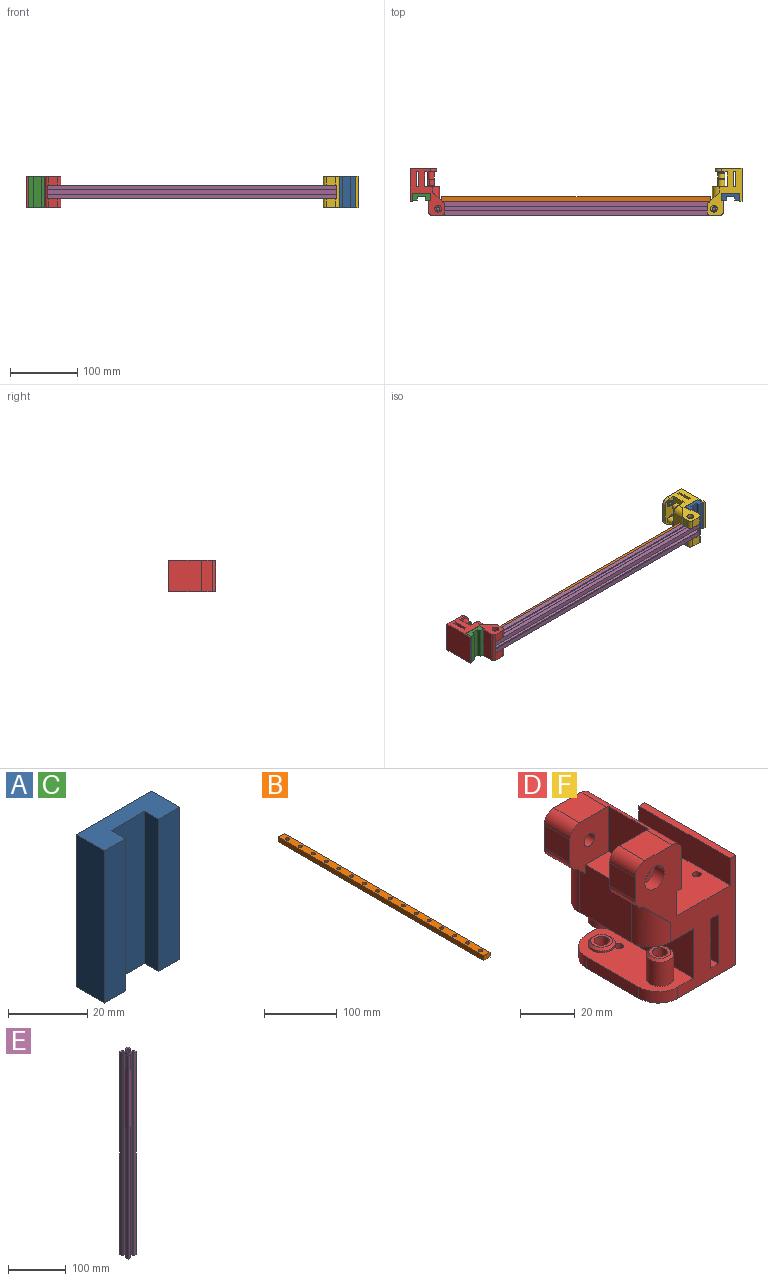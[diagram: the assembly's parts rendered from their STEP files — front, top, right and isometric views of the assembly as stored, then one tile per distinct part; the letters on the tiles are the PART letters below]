
ASSEMBLY  parts=6 mates=5
PART A: 18 faces, bbox 27x10x47 mm
  f0: plane 47x5mm, normal (-1,0,0), area 235mm2, adj f1,f7,f8,f9
  f1: plane 47x7.5mm, normal (0,-1,0), area 352.5mm2, adj f0,f2,f8,f9
  f2: plane 47x10mm, normal (1,0,0), area 470mm2, adj f1,f3,f8,f9
  f3: plane 47x27mm, normal (0,1,0), area 1240.7mm2, adj f2,f4,f8,f9,f10,f12,f14,f16
  f4: plane 47x10mm, normal (-1,0,0), area 470mm2, adj f3,f5,f8,f9
  f5: plane 47x7.5mm, normal (0,-1,0), area 352.5mm2, adj f4,f6,f8,f9
  f6: plane 47x5mm, normal (1,0,0), area 235mm2, adj f5,f7,f8,f9
  f7: plane 47x12mm, normal (0,-1,0), area 564mm2, adj f0,f6,f8,f9
  f8: plane 27x10mm, normal (0,0,1), area 210mm2, adj f0,f1,f2,f3,f4,f5,f6,f7
  f9: plane 27x10mm, normal (0,0,-1), area 210mm2, adj f0,f1,f2,f3,f4,f5,f6,f7
  f10: cylinder r=1.5mm len=3mm, axis (0,1,0), area 28.3mm2, adj f3,f11
  f11: plane 3x3mm, normal (0,1,0), area 7.1mm2, adj f10
  f12: cylinder r=1.5mm len=3mm, axis (0,1,0), area 28.3mm2, adj f3,f13
  f13: plane 3x3mm, normal (0,1,0), area 7.1mm2, adj f12
  f14: cylinder r=1.5mm len=3mm, axis (0,1,0), area 28.3mm2, adj f3,f15
  f15: plane 3x3mm, normal (0,1,0), area 7.1mm2, adj f14
  f16: cylinder r=1.5mm len=3mm, axis (0,1,0), area 28.3mm2, adj f3,f17
  f17: plane 3x3mm, normal (0,1,0), area 7.1mm2, adj f16
PART B: 22 faces, bbox 12x400x8 mm
  f0: plane 12x8mm, normal (0,1,0), area 96mm2, adj f1,f19,f20,f21
  f1: plane 400x8mm, normal (-1,0,0), area 3200mm2, adj f0,f2,f20,f21
  f2: plane 12x8mm, normal (0,-1,0), area 96mm2, adj f1,f19,f20,f21
  f3: cylinder r=2.75mm len=8mm, axis (0,0,-1), area 138.2mm2, adj f20,f21
  f4: cylinder r=2.75mm len=8mm, axis (0,0,-1), area 138.2mm2, adj f20,f21
  f5: cylinder r=2.75mm len=8mm, axis (0,0,-1), area 138.2mm2, adj f20,f21
  f6: cylinder r=2.75mm len=8mm, axis (0,0,-1), area 138.2mm2, adj f20,f21
  f7: cylinder r=2.75mm len=8mm, axis (0,0,-1), area 138.2mm2, adj f20,f21
  f8: cylinder r=2.75mm len=8mm, axis (0,0,-1), area 138.2mm2, adj f20,f21
  f9: cylinder r=2.75mm len=8mm, axis (0,0,-1), area 138.2mm2, adj f20,f21
  f10: cylinder r=2.75mm len=8mm, axis (0,0,-1), area 138.2mm2, adj f20,f21
  f11: cylinder r=2.75mm len=8mm, axis (0,0,-1), area 138.2mm2, adj f20,f21
  f12: cylinder r=2.75mm len=8mm, axis (0,0,-1), area 138.2mm2, adj f20,f21
  f13: cylinder r=2.75mm len=8mm, axis (0,0,-1), area 138.2mm2, adj f20,f21
  f14: cylinder r=2.75mm len=8mm, axis (0,0,-1), area 138.2mm2, adj f20,f21
  f15: cylinder r=2.75mm len=8mm, axis (0,0,-1), area 138.2mm2, adj f20,f21
  f16: cylinder r=2.75mm len=8mm, axis (0,0,-1), area 138.2mm2, adj f20,f21
  f17: cylinder r=2.75mm len=8mm, axis (0,0,-1), area 138.2mm2, adj f20,f21
  f18: cylinder r=2.75mm len=8mm, axis (0,0,-1), area 138.2mm2, adj f20,f21
  f19: plane 400x8mm, normal (1,0,0), area 3200mm2, adj f0,f2,f20,f21
  f20: plane 400x12mm, normal (0,0,1), area 4419.9mm2, adj f0,f1,f2,f3,f4,f5,f6,f7
  f21: plane 400x12mm, normal (0,0,-1), area 4419.9mm2, adj f0,f1,f2,f3,f4,f5,f6,f7
PART C: same geometry as A
PART D: 98 faces, bbox 52.1x47.2x70.2 mm
  f0: cylinder r=2.7mm len=8.3mm, axis (0,1,0), area 140.8mm2, adj f23,f95
  f1: cylinder r=2.7mm len=8.3mm, axis (0,1,0), area 140.8mm2, adj f21,f93
  f2: cylinder r=2.75mm len=14.8mm, axis (0,0,-1), area 255.7mm2, adj f83,f91
  f3: cylinder r=2.75mm len=5.5mm, axis (0,0,-1), area 82.9mm2, adj f85,f89
  f4: plane 4.93x2.67mm, normal (0,0,-1), area 9.7mm2, adj f20,f66,f67,f71
  f5: plane 4.93x2.67mm, normal (0,0,-1), area 9.7mm2, adj f20,f60,f61,f65
  f6: cylinder r=1.6mm len=5mm, axis (0,0,-1), area 50.3mm2, adj f14,f57
  f7: cylinder r=1.6mm len=5mm, axis (0,0,-1), area 50.3mm2, adj f14,f55
  f8: cylinder r=1.6mm len=5mm, axis (0,0,-1), area 50.3mm2, adj f14,f42
  f9: cylinder r=1.6mm len=5mm, axis (0,0,-1), area 50.3mm2, adj f14,f40
  f10: plane 47x4mm, normal (0,0,1), area 184.1mm2, adj f17,f18,f39,f41,f43,f44,f45,f47
  f11: plane 47x40mm, normal (0,0,-1), area 1607.7mm2, adj f17,f18,f30,f39,f41,f49,f50,f51
  f12: plane 47x21.95mm, normal (0,0,-1), area 785.1mm2, adj f17,f18,f31,f46,f52,f53,f54,f56
  f13: plane 47x4mm, normal (0,0,-1), area 184.1mm2, adj f17,f18,f39,f41,f43,f44,f45,f47
  f14: plane 47.2x27.6mm, normal (0,0,1), area 1238.8mm2, adj f6,f7,f8,f9,f17,f18,f20,f28
  f15: plane 14x13.3mm, normal (0,0,1), area 186.2mm2, adj f18,f23,f34,f36
  f16: plane 20.4x12mm, normal (0,0,1), area 244.8mm2, adj f21,f23,f27,f31
  f17: plane 70x51.9mm, normal (0,1,0), area 1457.8mm2, adj f10,f11,f12,f13,f14,f19,f20,f22
  f18: plane 70x51.9mm, normal (0,-1,0), area 1457.8mm2, adj f10,f11,f12,f13,f14,f15,f20,f24
  f19: plane 14x13.3mm, normal (0,0,1), area 186.2mm2, adj f17,f21,f34,f37
  f20: plane 47x11mm, normal (1,0,0), area 517mm2, adj f4,f5,f14,f17,f18,f25
  f21: plane 24.2x20mm, normal (0,-1,0), area 378.8mm2, adj f1,f16,f19,f22,f27,f31,f32,f34
  f22: plane 13.3x10.3mm, normal (-1,0,0), area 137mm2, adj f17,f21,f37,f38
  f23: plane 24.2x20mm, normal (0,1,0), area 378.8mm2, adj f0,f15,f16,f24,f27,f31,f33,f34
  f24: plane 13.3x10.3mm, normal (-1,0,0), area 137mm2, adj f18,f23,f35,f36
  f25: plane 47x2.5mm, normal (0,0,-1), area 117.5mm2, adj f17,f18,f20,f26
  f26: plane 47x17mm, normal (1,0,0), area 799mm2, adj f17,f18,f25,f34
  f27: plane 20.4x20.1mm, normal (-1,0,0), area 410mm2, adj f16,f21,f23,f34
  f28: plane 47x12mm, normal (-1,0,0), area 564mm2, adj f14,f17,f18,f29
  f29: plane 47x3mm, normal (0,0,1), area 141mm2, adj f17,f18,f28,f30
  f30: plane 49x47mm, normal (1,0,0), area 2303mm2, adj f11,f17,f18,f29
  f31: plane 27x22.8mm, normal (-1,0,0), area 589.2mm2, adj f12,f16,f21,f23,f32,f33,f52,f53
  f32: plane 14x14mm, normal (-0.71,0,-0.71), area 105.6mm2, adj f17,f21,f31,f38,f52
  f33: plane 14x14mm, normal (-0.71,0,-0.71), area 105.6mm2, adj f18,f23,f31,f35,f53
  f34: cylinder r=5mm len=47mm, axis (0,-1,0), area 348.6mm2, adj f15,f17,f18,f19,f21,f23,f26,f27
  f35: cylinder r=5mm len=13.3mm, axis (0,1,0), area 91.1mm2, adj f18,f23,f24,f33
  f36: cylinder r=5mm len=13.3mm, axis (0,-1,0), area 104.5mm2, adj f15,f18,f23,f24
  f37: cylinder r=5mm len=13.3mm, axis (0,-1,0), area 104.5mm2, adj f17,f19,f21,f22
  f38: cylinder r=5mm len=13.3mm, axis (0,1,0), area 91.1mm2, adj f17,f21,f22,f32
  f39: cylinder r=3mm len=32mm, axis (0,0,-1), area 509.5mm2, adj f10,f11,f13,f40,f44,f45
  f40: plane 6x6mm, normal (0,0,-1), area 20.2mm2, adj f9,f39
  f41: cylinder r=3mm len=32mm, axis (0,0,-1), area 509.5mm2, adj f10,f11,f13,f42,f43,f45
  f42: plane 6x6mm, normal (0,0,-1), area 20.2mm2, adj f8,f41
  f43: plane 22x11.54mm, normal (-1,0,0), area 254mm2, adj f10,f13,f17,f41
  f44: plane 22x11.54mm, normal (-1,0,0), area 254mm2, adj f10,f13,f18,f39
  f45: plane 22x16.09mm, normal (-1,0,0), area 354mm2, adj f10,f13,f39,f41
  f46: plane 47x22mm, normal (-1,0,0), area 1034mm2, adj f12,f17,f18,f48
  f47: plane 47x22mm, normal (1,0,0), area 1034mm2, adj f10,f13,f17,f18
  f48: plane 47x18.05mm, normal (0,0,1), area 632.6mm2, adj f17,f18,f46,f49,f50,f51,f82,f84
  f49: plane 27x5mm, normal (-1,0,0), area 135mm2, adj f11,f48,f50,f51
  f50: cylinder r=10mm len=10mm, axis (0,0,-1), area 78.5mm2, adj f11,f18,f48,f49
  f51: cylinder r=10mm len=10mm, axis (0,0,1), area 78.5mm2, adj f11,f17,f48,f49
  f52: cylinder r=10mm len=18.8mm, axis (0,0,1), area 238.2mm2, adj f12,f17,f31,f32
  f53: cylinder r=10mm len=18.8mm, axis (0,0,-1), area 238.2mm2, adj f12,f18,f31,f33
  f54: cylinder r=3mm len=7mm, axis (0,0,-1), area 103.5mm2, adj f12,f55,f73,f75,f76
  f55: plane 6x6mm, normal (0,0,-1), area 20.2mm2, adj f7,f54
  f56: cylinder r=3mm len=17mm, axis (0,0,-1), area 155.2mm2, adj f12,f57,f78,f80,f81
  f57: plane 6x6mm, normal (0,0,-1), area 20.2mm2, adj f6,f56
  f58: cone r=2.6mm half-angle=45deg, axis (0,0,-1), area 15.5mm2, adj f69,f70,f72
  f59: cone r=2.6mm half-angle=45deg, axis (0,0,-1), area 15.5mm2, adj f63,f64,f77
  f60: bspline ~9.98x6.08mm, area 89.2mm2, adj f5,f14,f62,f63,f64,f65
  f61: bspline ~9.98x6.08mm, area 89.4mm2, adj f5,f14,f62,f63,f64,f65
  f62: bspline ~9.7x6.16mm, area 22.7mm2, adj f14,f60,f61,f63
  f63: plane 1.96x1.93mm, normal (0,0,1), area 0.1mm2, adj f59,f60,f61,f62
  f64: plane 5.4x5.4mm, normal (0,0,-1), area 3.3mm2, adj f59,f60,f61,f65
  f65: cylinder r=2.2mm len=9.4mm, axis (0,0,1), area 35.5mm2, adj f5,f60,f61,f64
  f66: bspline ~9.98x6.08mm, area 89.2mm2, adj f4,f14,f68,f69,f70,f71
  f67: bspline ~9.98x6.08mm, area 89.4mm2, adj f4,f14,f68,f69,f70,f71
  f68: bspline ~9.7x6.16mm, area 22.7mm2, adj f14,f66,f67,f69
  f69: plane 1.96x1.93mm, normal (0,0,1), area 0.1mm2, adj f58,f66,f67,f68
  f70: plane 5.4x5.4mm, normal (0,0,-1), area 3.3mm2, adj f58,f66,f67,f71
  f71: cylinder r=2.2mm len=9.4mm, axis (0,0,1), area 35.5mm2, adj f4,f66,f67,f70
  f72: plane 6.4x6.4mm, normal (0,0,1), area 3.9mm2, adj f58,f74
  f73: cylinder r=5mm len=10mm, axis (0,0,1), area 26.7mm2, adj f12,f54,f76
  f74: cylinder r=3mm len=6mm, axis (0,0,1), area 37.7mm2, adj f72,f75
  f75: plane 8x8mm, normal (0,0,-1), area 20.9mm2, adj f54,f74,f76
  f76: cone r=4mm half-angle=45deg, axis (0,0,1), area 34.7mm2, adj f54,f73,f75
  f77: plane 6.4x6.4mm, normal (0,0,1), area 3.9mm2, adj f59,f79
  f78: cylinder r=5mm len=11mm, axis (0,0,1), area 293.5mm2, adj f12,f56,f81
  f79: cylinder r=3mm len=12mm, axis (0,0,1), area 226.2mm2, adj f77,f80
  f80: plane 8x8mm, normal (0,0,-1), area 20.9mm2, adj f56,f79,f81
  f81: cone r=4mm half-angle=45deg, axis (0,0,1), area 34.7mm2, adj f56,f78,f80
  f82: cylinder r=5mm len=13.8mm, axis (0,0,-1), area 343.4mm2, adj f48,f86,f91,f96
  f83: plane 8x8mm, normal (0,0,1), area 26.5mm2, adj f2,f86
  f84: cylinder r=5mm len=10mm, axis (0,0,-1), area 29.2mm2, adj f48,f87,f89,f97
  f85: plane 8x8mm, normal (0,0,1), area 26.5mm2, adj f3,f87
  f86: cone r=5mm half-angle=45deg, axis (0,0,-1), area 40mm2, adj f82,f83
  f87: cone r=5mm half-angle=45deg, axis (0,0,-1), area 40mm2, adj f84,f85
  f88: cylinder r=5mm len=10mm, axis (0,0,-1), area 60.1mm2, adj f11,f89,f97
  f89: plane 10x10mm, normal (0,0,-1), area 54.8mm2, adj f3,f84,f88
  f90: cylinder r=5mm len=10mm, axis (0,0,-1), area 60.1mm2, adj f11,f91,f96
  f91: plane 10x10mm, normal (0,0,-1), area 54.8mm2, adj f2,f82,f90
  f92: cylinder r=5mm len=10mm, axis (0,1,0), area 157.1mm2, adj f17,f93
  f93: plane 10x10mm, normal (0,1,0), area 55.6mm2, adj f1,f92
  f94: cylinder r=5mm len=10mm, axis (0,-1,0), area 157.1mm2, adj f18,f95
  f95: plane 10x10mm, normal (0,-1,0), area 55.6mm2, adj f0,f94
  f96: cylinder r=1.6mm len=5mm, axis (0,0,1), area 43.3mm2, adj f11,f48,f82,f90
  f97: cylinder r=1.6mm len=5mm, axis (0,0,1), area 43.3mm2, adj f11,f48,f84,f88
PART E: 47 faces, bbox 20x20x430 mm
  f0: plane 430x1.5mm, normal (0,1,0), area 645mm2, adj f1,f43,f45,f46
  f1: plane 430x6.9mm, normal (-1,0,0), area 2967mm2, adj f0,f2,f45,f46
  f2: plane 430x6.9mm, normal (0,-1,0), area 2967mm2, adj f1,f3,f45,f46
  f3: plane 430x1.5mm, normal (1,0,0), area 645mm2, adj f2,f4,f45,f46
  f4: plane 430x3.1mm, normal (0,1,0), area 1333mm2, adj f3,f5,f45,f46
  f5: plane 430x1mm, normal (1,0,0), area 430mm2, adj f4,f6,f45,f46
  f6: plane 430x3.5mm, normal (0.75,-0.66,0), area 2010.5mm2, adj f5,f7,f45,f46
  f7: plane 430x6.2mm, normal (0,-1,0), area 2666mm2, adj f6,f8,f45,f46
  f8: plane 430x3.5mm, normal (-0.75,-0.66,0), area 2010.5mm2, adj f7,f9,f45,f46
  f9: plane 430x1mm, normal (-1,0,0), area 430mm2, adj f8,f10,f45,f46
  f10: plane 430x3.1mm, normal (0,1,0), area 1333mm2, adj f9,f11,f45,f46
  f11: plane 430x1.5mm, normal (-1,0,0), area 645mm2, adj f10,f12,f45,f46
  f12: plane 430x6.9mm, normal (0,-1,0), area 2967mm2, adj f11,f13,f45,f46
  f13: plane 430x6.9mm, normal (1,0,0), area 2967mm2, adj f12,f14,f45,f46
  f14: plane 430x1.5mm, normal (0,1,0), area 645mm2, adj f13,f15,f45,f46
  f15: plane 430x3.1mm, normal (-1,0,0), area 1333mm2, adj f14,f16,f45,f46
  f16: plane 430x1mm, normal (0,1,0), area 430mm2, adj f15,f17,f45,f46
  f17: plane 430x3.5mm, normal (0.66,0.75,0), area 2010.5mm2, adj f16,f18,f45,f46
  f18: plane 430x6.2mm, normal (1,0,0), area 2666mm2, adj f17,f19,f45,f46
  f19: plane 430x3.5mm, normal (0.66,-0.75,0), area 2010.5mm2, adj f18,f20,f45,f46
  f20: plane 430x1mm, normal (0,-1,0), area 430mm2, adj f19,f21,f45,f46
  f21: plane 430x3.1mm, normal (-1,0,0), area 1333mm2, adj f20,f22,f45,f46
  f22: plane 430x1.5mm, normal (0,-1,0), area 645mm2, adj f21,f23,f45,f46
  f23: plane 430x6.9mm, normal (1,0,0), area 2967mm2, adj f22,f24,f45,f46
  f24: plane 430x6.9mm, normal (0,1,0), area 2967mm2, adj f23,f25,f45,f46
  f25: plane 430x1.5mm, normal (-1,0,0), area 645mm2, adj f24,f26,f45,f46
  f26: plane 430x3.1mm, normal (0,-1,0), area 1333mm2, adj f25,f27,f45,f46
  f27: plane 430x1mm, normal (-1,0,0), area 430mm2, adj f26,f28,f45,f46
  f28: plane 430x3.5mm, normal (-0.75,0.66,0), area 2010.5mm2, adj f27,f29,f45,f46
  f29: plane 430x6.2mm, normal (0,1,0), area 2666mm2, adj f28,f30,f45,f46
  f30: plane 430x3.5mm, normal (0.75,0.66,0), area 2010.5mm2, adj f29,f31,f45,f46
  f31: plane 430x1mm, normal (1,0,0), area 430mm2, adj f30,f32,f45,f46
  f32: plane 430x3.1mm, normal (0,-1,0), area 1333mm2, adj f31,f33,f45,f46
  f33: plane 430x1.5mm, normal (1,0,0), area 645mm2, adj f32,f34,f45,f46
  f34: plane 430x6.9mm, normal (0,1,0), area 2967mm2, adj f33,f35,f45,f46
  f35: plane 430x6.9mm, normal (-1,0,0), area 2967mm2, adj f34,f36,f45,f46
  f36: plane 430x1.5mm, normal (0,-1,0), area 645mm2, adj f35,f37,f45,f46
  f37: plane 430x3.1mm, normal (1,0,0), area 1333mm2, adj f36,f38,f45,f46
  f38: plane 430x1mm, normal (0,-1,0), area 430mm2, adj f37,f39,f45,f46
  f39: plane 430x3.5mm, normal (-0.66,-0.75,0), area 2010.5mm2, adj f38,f40,f45,f46
  f40: plane 430x6.2mm, normal (-1,0,0), area 2666mm2, adj f39,f41,f45,f46
  f41: plane 430x3.5mm, normal (-0.66,0.75,0), area 2010.5mm2, adj f40,f42,f45,f46
  f42: plane 430x1mm, normal (0,1,0), area 430mm2, adj f41,f43,f45,f46
  f43: plane 430x3.1mm, normal (1,0,0), area 1333mm2, adj f0,f42,f45,f46
  f44: cylinder r=2.75mm len=430mm, axis (0,0,-1), area 7429.9mm2, adj f45,f46
  f45: plane 20x20mm, normal (0,0,1), area 159.2mm2, adj f0,f1,f2,f3,f4,f5,f6,f7
  f46: plane 20x20mm, normal (0,0,-1), area 159.2mm2, adj f0,f1,f2,f3,f4,f5,f6,f7
PART F: same geometry as D
PLACE A t=(-122.15,86.18,102.71)mm
PLACE B rot(axis=(0.58,0.58,-0.58),120deg) t=(-352.35,86.33,126.21)mm
PLACE C rot(axis=(0,1,0),180deg) t=(-582.55,86.18,149.71)mm
PLACE D rot(axis=(0,-0.71,0.71),180deg) t=(-582.55,96.18,126.21)mm
PLACE E rot(axis=(0.58,0.58,0.58),120deg) t=(-567.35,68.33,126.21)mm
PLACE F rot(axis=(1,0,0),90deg) t=(-122.15,96.18,126.21)mm
MATE fastened F.f27 <-> E.f44  axis (-1,0,0) through (-137.35,68.33,126.21)mm
MATE fastened D.f27 <-> E.f44  axis (1,0,0) through (-567.35,68.33,126.21)mm
MATE fastened B.f20 <-> E.f13  axis (0,-1,0) through (-352.35,78.33,126.21)mm
MATE fastened C.f10 <-> D.f8  axis (0,1,0) through (-592.55,91.18,116.21)mm
MATE fastened A.f10 <-> F.f8  axis (0,1,0) through (-112.15,91.18,136.21)mm
